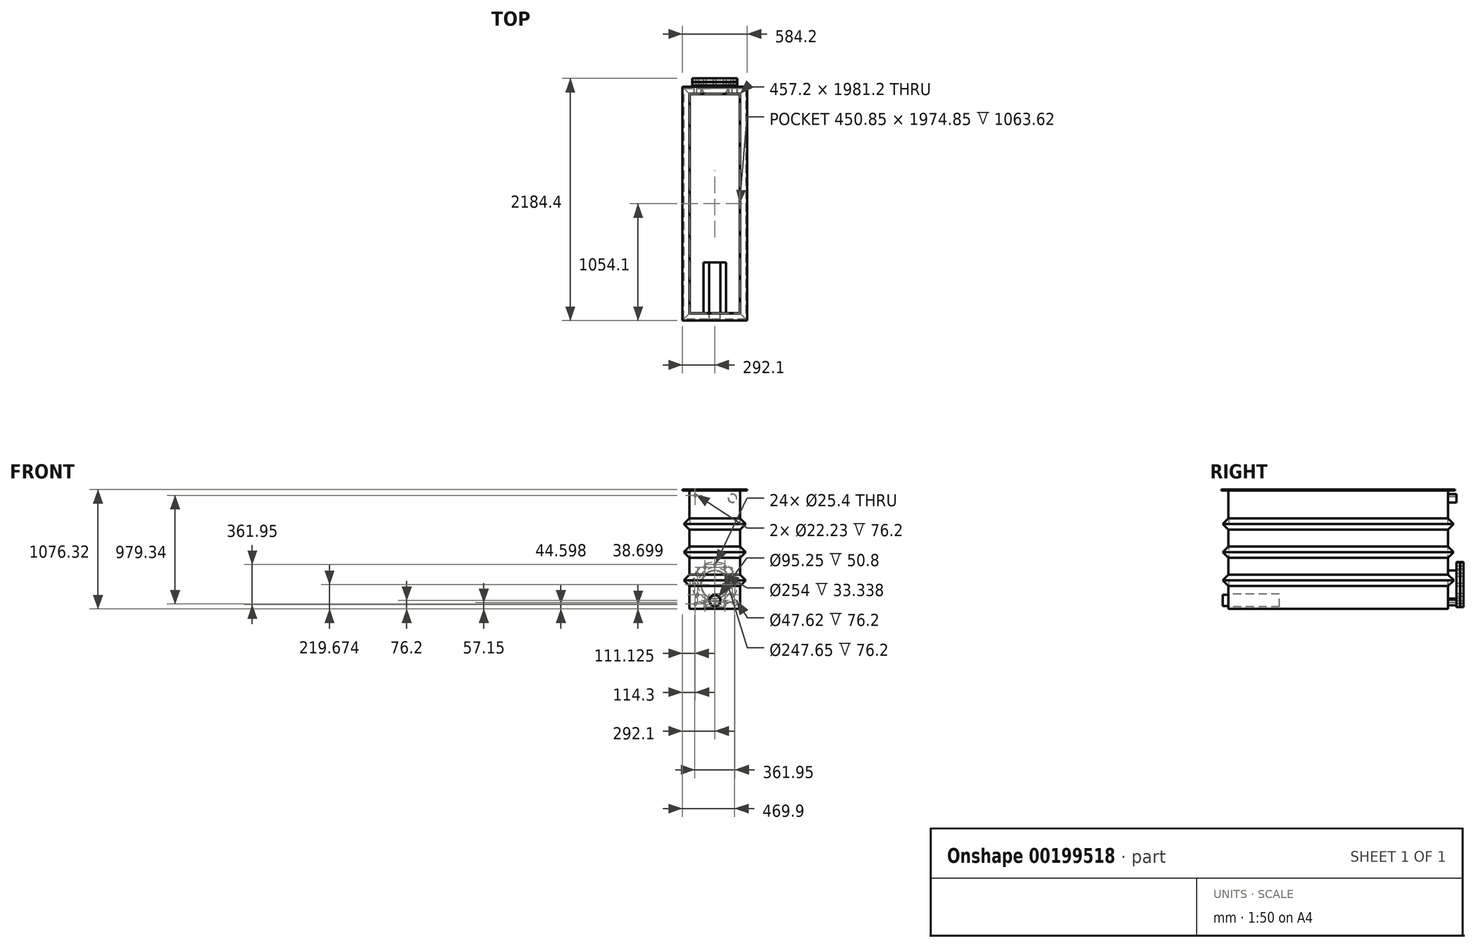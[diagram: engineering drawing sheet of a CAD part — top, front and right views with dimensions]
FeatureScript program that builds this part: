
annotation { "Feature Type Name" : "Feature", "Feature Type Description" : "" }
export const myFeature = defineFeature(function(context is Context, id is Id, definition is map)
    precondition{}
    {
        {
            var Q0;
            Q0=qCreatedBy(makeId("Right.planeOp"),FACE);
            var sketch = newSketch(context, id + "F0", { "sketchPlane" : qUnion([Q0])});
            skLineSegment(sketch, "E0.bottom", {"start": v(-990.6, 533.4) * mm, "end": v(990.6, 533.4) * mm});
            skLineSegment(sketch, "E0.top", {"start": v(-990.6, -533.4) * mm, "end": v(990.6, -533.4) * mm});
            skLineSegment(sketch, "E0.left", {"start": v(-990.6, 533.4) * mm, "end": v(-990.6, -533.4) * mm});
            skLineSegment(sketch, "E0.right", {"start": v(990.6, 533.4) * mm, "end": v(990.6, -533.4) * mm});
            skSolve(sketch);
        }
        {
            var Q0;
            Q0=makeQuery(id+"F0.imprint","IMPRINT",FACE,{"disambiguationData":[TD([[makeQuery(id+"F0.imprint","IMPRINT",EDGE,{"derivedFrom":sQuery(id+"F0.wireOp",EDGE,"E0.bottom")}),-1.0]])]});
            extrude(context, id + "F1", {"entities" : qUnion([Q0]), "endBound" : BoundingType.SYMMETRIC, "depth" : 457.2 * mm, "hasSecondDirection" : true, "secondDirectionOppositeDirection" : true, "secondDirectionDepth" : 228.6 * mm});
        }
        {
            var Q0;
            Q0=makeQuery(id+"F1.opExtrude","SWEPT_FACE",FACE,{"disambiguationData":[OSD([sQuery(id+"F0.wireOp",EDGE,"E0.bottom")])]});
            shell(context, id + "F2", {"entities" : qUnion([Q0]), "thickness" : 3.17 * mm});
        }
        {
            var Q0;
            Q0=makeQuery(id+"F1.opExtrude","SWEPT_FACE",FACE,{"disambiguationData":[OSD([sQuery(id+"F0.wireOp",EDGE,"E0.left")])]});
            var sketch = newSketch(context, id + "F3", { "sketchPlane" : qUnion([Q0])});
            skCircle(sketch, "E1", {"center": v(0, -457.2) * mm, "radius": 50.8 * mm});
            skCircle(sketch, "E2", {"center": v(0, -457.2) * mm, "radius": 47.63 * mm});
            skLineSegment(sketch, "E3", {"start": v(-571.69, -330.2) * mm, "end": v(666.68, -330.2) * mm, "construction": true});
            skSolve(sketch);
        }
        {
            var Q0;
            Q0 = qSketchRegion(id + "F3", true);
            extrude(context, id + "F4", {"entities" : qUnion([Q0]), "depth" : 50.8 * mm});
        }
        {
            var Q0;
            Q0=makeQuery(id+"F2.opShell","OFFSET_FACE",FACE,{"disambiguationData":[OSD([sQuery(id+"F0.wireOp",EDGE,"E0.left")])]});
            var sketch = newSketch(context, id + "F5", { "sketchPlane" : qUnion([Q0])});
            skPoint(sketch, "E4", {"position": v(0, -457.2) * mm});
            skCircle(sketch, "E5", {"center": v(0, -457.2) * mm, "radius": 38.1 * mm, "construction": true});
            skLineSegment(sketch, "E6", {"start": v(-101.6, -514.35) * mm, "end": v(-50.8, -400.05) * mm});
            skLineSegment(sketch, "E7", {"start": v(-50.8, -400.05) * mm, "end": v(50.8, -400.05) * mm});
            skLineSegment(sketch, "E8", {"start": v(50.8, -400.05) * mm, "end": v(101.6, -514.35) * mm});
            skLineSegment(sketch, "E9", {"start": v(101.6, -514.35) * mm, "end": v(-101.6, -514.35) * mm});
            skSolve(sketch);
        }
        {
            var Q0;
            Q0=makeQuery(id+"F5.imprint","IMPRINT",FACE,{"disambiguationData":[TD([[makeQuery(id+"F5.imprint","IMPRINT",EDGE,{"derivedFrom":sQuery(id+"F5.wireOp",EDGE,"E6")}),-1.0]])]});
            extrude(context, id + "F6", {"entities" : qUnion([Q0]), "operationType" : NewBodyOperationType.ADD, "depth" : 457.2 * mm});
        }
        {
            var Q0;
            Q0=makeQuery(id+"F1.opExtrude","SWEPT_FACE",FACE,{"disambiguationData":[OSD([sQuery(id+"F0.wireOp",EDGE,"E0.right")])]});
            var sketch = newSketch(context, id + "F7", { "sketchPlane" : qUnion([Q0])});
            skPoint(sketch, "E10", {"position": v(0, -313.73) * mm});
            skCircle(sketch, "E11", {"center": v(0, -313.73) * mm, "radius": 127 * mm});
            skCircle(sketch, "E12", {"center": v(0, -313.73) * mm, "radius": 123.83 * mm});
            skSolve(sketch);
        }
        {
            var Q0;
            Q0 = qSketchRegion(id + "F7", true);
            extrude(context, id + "F8", {"entities" : qUnion([Q0]), "operationType" : NewBodyOperationType.ADD, "depth" : 76.2 * mm});
        }
        {
            var Q0;
            Q0=makeQuery(id+"F8.opExtrude","CAP_FACE",FACE,{"disambiguationData":[OSD([sQuery(id+"F7.wireOp",EDGE,"E11"),sQuery(id+"F7.wireOp",EDGE,"E12")])],"isStart":false});
            var sketch = newSketch(context, id + "F9", { "sketchPlane" : qUnion([Q0])});
            skPoint(sketch, "E13", {"position": v(0, -313.73) * mm});
            skCircle(sketch, "E14", {"center": v(0, -313.73) * mm, "radius": 203.2 * mm});
            skCircle(sketch, "E15", {"center": v(0, -313.73) * mm, "radius": 123.83 * mm});
            skSolve(sketch);
        }
        {
            var Q0;
            Q0=makeQuery(id+"F9.imprint","IMPRINT",FACE,{"disambiguationData":[TD([[makeQuery(id+"F9.imprint","IMPRINT",EDGE,{"derivedFrom":sQuery(id+"F9.wireOp",EDGE,"E14")}),1.0]])]});
            extrude(context, id + "F10", {"entities" : qUnion([Q0]), "depth" : 30.16 * mm});
        }
        {
            var Q0;
            Q0=makeQuery(id+"F10.opExtrude","CAP_FACE",FACE,{"disambiguationData":[OSD([sQuery(id+"F7.wireOp",EDGE,"E11"),sQuery(id+"F9.wireOp",EDGE,"E14")])],"isStart":false});
            var sketch = newSketch(context, id + "F11", { "sketchPlane" : qUnion([Q0])});
            skPoint(sketch, "E16", {"position": v(0, -313.73) * mm});
            skCircle(sketch, "E17", {"center": v(0, -132.75) * mm, "radius": 12.7 * mm});
            skCircle(sketch, "E18.1.0", {"center": v(-90.49, -157) * mm, "radius": 12.7 * mm});
            skCircle(sketch, "E18.2.0", {"center": v(-156.73, -223.24) * mm, "radius": 12.7 * mm});
            skCircle(sketch, "E18.3.0", {"center": v(-180.98, -313.73) * mm, "radius": 12.7 * mm});
            skCircle(sketch, "E18.4.0", {"center": v(-156.73, -404.21) * mm, "radius": 12.7 * mm});
            skCircle(sketch, "E18.5.0", {"center": v(-90.49, -470.45) * mm, "radius": 12.7 * mm});
            skCircle(sketch, "E18.6.0", {"center": v(0, -494.7) * mm, "radius": 12.7 * mm});
            skCircle(sketch, "E18.7.0", {"center": v(90.49, -470.45) * mm, "radius": 12.7 * mm});
            skCircle(sketch, "E18.8.0", {"center": v(156.73, -404.21) * mm, "radius": 12.7 * mm});
            skCircle(sketch, "E18.9.0", {"center": v(180.98, -313.73) * mm, "radius": 12.7 * mm});
            skCircle(sketch, "E19.1.10.0", {"center": v(156.73, -223.24) * mm, "radius": 12.7 * mm});
            skCircle(sketch, "E19.1.11.0", {"center": v(90.49, -157) * mm, "radius": 12.7 * mm});
            skSolve(sketch);
        }
        {
            var Q0;
            Q0 = qSketchRegion(id + "F11", true);
            extrude(context, id + "F12", {"entities" : qUnion([Q0]), "operationType" : NewBodyOperationType.REMOVE, "endBound" : BoundingType.UP_TO_NEXT, "oppositeDirection" : true, "depth" : 25.4 * mm});
        }
        {
            var Q0;
            Q0=makeQuery(id+"F10.opExtrude","CAP_FACE",FACE,{"disambiguationData":[OSD([sQuery(id+"F7.wireOp",EDGE,"E11"),sQuery(id+"F9.wireOp",EDGE,"E14")])],"isStart":false});
            var sketch = newSketch(context, id + "F13", { "sketchPlane" : qUnion([Q0])});
            skSolve(sketch);
        }
        {
            var Q0;
            Q0=makeQuery(id+"F13.imprint","IMPRINT",FACE,{"disambiguationData":[TD([[makeQuery(id+"F13.imprint","IMPRINT",EDGE,{"derivedFrom":makeQuery(id+"F10.opExtrude","CAP_EDGE",EDGE,{"disambiguationData":[OSD([sQuery(id+"F9.wireOp",EDGE,"E14")])],"isStart":false})}),1.0]])]});
            var sketch = newSketch(context, id + "F14", { "sketchPlane" : qUnion([Q0])});
            skPoint(sketch, "E20", {"position": v(0, -313.73) * mm});
            skCircle(sketch, "E21", {"center": v(0, -313.73) * mm, "radius": 127 * mm});
            skCircle(sketch, "E22", {"center": v(0, -313.73) * mm, "radius": 152.4 * mm});
            skSolve(sketch);
        }
        {
            var Q0;
            Q0 = qSketchRegion(id + "F14", true);
            extrude(context, id + "F15", {"entities" : qUnion([Q0]), "operationType" : NewBodyOperationType.ADD, "depth" : 3.17 * mm});
        }
        {
            var Q0;
            Q0=makeQuery(id+"F15.opExtrude","CAP_FACE",FACE,{"disambiguationData":[OSD([sQuery(id+"F14.wireOp",EDGE,"E21"),sQuery(id+"F14.wireOp",EDGE,"E22")])],"isStart":false});
            var sketch = newSketch(context, id + "F16", { "sketchPlane" : qUnion([Q0])});
            skPoint(sketch, "E23", {"position": v(0, -313.73) * mm});
            skCircle(sketch, "E24", {"center": v(0, -313.73) * mm, "radius": 203.2 * mm});
            skSolve(sketch);
        }
        {
            var Q0;
            Q0 = qSketchRegion(id + "F16", true);
            extrude(context, id + "F17", {"entities" : qUnion([Q0]), "operationType" : NewBodyOperationType.ADD, "depth" : 30.16 * mm});
        }
        {
            var Q0;
            Q0=makeQuery(id+"F17.opExtrude","CAP_FACE",FACE,{"disambiguationData":[OSD([sQuery(id+"F16.wireOp",EDGE,"E24")])],"isStart":false});
            var sketch = newSketch(context, id + "F18", { "sketchPlane" : qUnion([Q0])});
            skPoint(sketch, "E25", {"position": v(0, -313.73) * mm});
            skCircle(sketch, "E26", {"center": v(0, -132.75) * mm, "radius": 12.7 * mm});
            skCircle(sketch, "E27.1.0", {"center": v(-90.49, -157) * mm, "radius": 12.7 * mm});
            skCircle(sketch, "E27.2.0", {"center": v(-156.73, -223.24) * mm, "radius": 12.7 * mm});
            skCircle(sketch, "E27.3.0", {"center": v(-180.98, -313.73) * mm, "radius": 12.7 * mm});
            skCircle(sketch, "E27.4.0", {"center": v(-156.73, -404.21) * mm, "radius": 12.7 * mm});
            skCircle(sketch, "E27.5.0", {"center": v(-90.49, -470.45) * mm, "radius": 12.7 * mm});
            skCircle(sketch, "E27.6.0", {"center": v(0, -494.7) * mm, "radius": 12.7 * mm});
            skCircle(sketch, "E27.7.0", {"center": v(90.49, -470.45) * mm, "radius": 12.7 * mm});
            skCircle(sketch, "E27.8.0", {"center": v(156.73, -404.21) * mm, "radius": 12.7 * mm});
            skCircle(sketch, "E27.9.0", {"center": v(180.98, -313.73) * mm, "radius": 12.7 * mm});
            skCircle(sketch, "E28.1.10.0", {"center": v(156.73, -223.24) * mm, "radius": 12.7 * mm});
            skCircle(sketch, "E28.1.11.0", {"center": v(90.49, -157) * mm, "radius": 12.7 * mm});
            skSolve(sketch);
        }
        {
            var Q0;
            Q0 = qSketchRegion(id + "F18", true);
            extrude(context, id + "F19", {"entities" : qUnion([Q0]), "operationType" : NewBodyOperationType.REMOVE, "endBound" : BoundingType.UP_TO_NEXT, "oppositeDirection" : true, "depth" : 25.4 * mm});
        }
        {
            var Q0;
            {var subQ1=sQuery(id+"F0.wireOp",EDGE,"E0.right");var subQ3=sQuery(id+"F0.wireOp",EDGE,"E0.bottom");Q0=makeQuery(id+"F8.boolean.opBoolean","SPLIT",FACE,{"disambiguationData":[TD([makeQuery(id+"F1.opExtrude","SWEPT_FACE",FACE,{"disambiguationData":[OSD([subQ3])]})])],"derivedFrom":makeQuery(id+"F1.opExtrude","SWEPT_FACE",FACE,{"disambiguationData":[OSD([subQ1])]})});}
            var sketch = newSketch(context, id + "F20", { "sketchPlane" : qUnion([Q0])});
            skPoint(sketch, "E29", {"position": v(0, -409.57) * mm});
            skPoint(sketch, "E30", {"position": v(-158.75, 465.14) * mm});
            skCircle(sketch, "E31", {"center": v(-158.75, 465.14) * mm, "radius": 38.1 * mm});
            skCircle(sketch, "E32", {"center": v(-158.75, 465.14) * mm, "radius": 36.51 * mm});
            skPoint(sketch, "E33", {"position": v(-158.75, 428.63) * mm});
            skCircle(sketch, "E34", {"center": v(-177.8, -476.25) * mm, "radius": 25.4 * mm});
            skCircle(sketch, "E35", {"center": v(-177.8, -476.25) * mm, "radius": 23.81 * mm});
            skCircle(sketch, "E36", {"center": v(177.8, 490.54) * mm, "radius": 12.7 * mm});
            skCircle(sketch, "E37", {"center": v(177.8, 490.54) * mm, "radius": 11.11 * mm});
            skCircle(sketch, "E38", {"center": v(177.8, -488.8) * mm, "radius": 12.7 * mm});
            skCircle(sketch, "E39", {"center": v(177.8, -488.8) * mm, "radius": 11.11 * mm});
            skLineSegment(sketch, "E40", {"start": v(-180.53, -501.5) * mm, "end": v(332.18, -501.5) * mm, "construction": true});
            skLineSegment(sketch, "E41", {"start": v(-158.75, 503.24) * mm, "end": v(393.96, 503.24) * mm, "construction": true});
            skLineSegment(sketch, "E42", {"start": v(-158.75, 465.14) * mm, "end": v(-158.75, 301.65) * mm, "construction": true});
            skSolve(sketch);
        }
        {
            var Q0;
            Q0 = qSketchRegion(id + "F20", true);
            extrude(context, id + "F21", {"entities" : qUnion([Q0]), "operationType" : NewBodyOperationType.ADD, "depth" : 76.2 * mm});
        }
        {
            var Q0;
            Q0=makeQuery(id+"F2.opShell","OFFSET_FACE",FACE,{"disambiguationData":[OSD([sQuery(id+"F0.wireOp",EDGE,"E0.top")])]});
            cPlane(context, id + "F22", {"entities" : qUnion([Q0]), "cplaneType" : CPlaneType.OFFSET, "offset" : 254 * mm, "width" : 152.4 * mm, "height" : 152.4 * mm});
        }
        {
            var Q0;
            Q0=qCreatedBy(id+"F22.planeOp",FACE);
            var sketch = newSketch(context, id + "F23", { "sketchPlane" : qUnion([Q0])});
            skPoint(sketch, "E43", {"position": v(-225.43, 987.43) * mm});
            skPoint(sketch, "E44", {"position": v(228.6, 990.6) * mm});
            skPoint(sketch, "E45", {"position": v(228.6, -990.6) * mm});
            skPoint(sketch, "E46", {"position": v(-228.6, -990.6) * mm});
            skLineSegment(sketch, "E47", {"start": v(-228.6, -990.6) * mm, "end": v(-225.42, 987.43) * mm});
            skLineSegment(sketch, "E48", {"start": v(228.6, 990.6) * mm, "end": v(228.6, -990.6) * mm});
            skLineSegment(sketch, "E49", {"start": v(-225.42, 987.43) * mm, "end": v(228.6, 990.6) * mm});
            skLineSegment(sketch, "E50", {"start": v(-228.6, -990.6) * mm, "end": v(228.6, -990.6) * mm});
            skSolve(sketch);
        }
        {
            var Q0;
            Q0=makeQuery(id+"F1.opExtrude","SWEPT_FACE",FACE,{"disambiguationData":[OSD([sQuery(id+"F0.wireOp",EDGE,"E0.left")])]});
            var sketch = newSketch(context, id + "F24", { "sketchPlane" : qUnion([Q0])});
            skLineSegment(sketch, "E51", {"start": v(-228.6, -276.22) * mm, "end": v(-228.6, -327.02) * mm});
            skLineSegment(sketch, "E52", {"start": v(-228.6, -327.02) * mm, "end": v(-279.4, -276.22) * mm});
            skLineSegment(sketch, "E53", {"start": v(-279.4, -276.22) * mm, "end": v(-228.6, -225.42) * mm});
            skLineSegment(sketch, "E54", {"start": v(-228.6, -225.42) * mm, "end": v(-228.6, -276.22) * mm});
            skSolve(sketch);
        }
        {
            var Q0;
            Q0=makeQuery(id+"F24.imprint","IMPRINT",FACE,{"disambiguationData":[TD([[makeQuery(id+"F24.imprint","IMPRINT",EDGE,{"derivedFrom":sQuery(id+"F24.wireOp",EDGE,"E51")}),-1.0]])]});
            var Q1;
            Q1=sQuery(id+"F23.wireOp",EDGE,"E47");
            var Q2;
            Q2=sQuery(id+"F23.wireOp",EDGE,"E49");
            var Q3;
            Q3=sQuery(id+"F23.wireOp",EDGE,"E48");
            var Q4;
            Q4=sQuery(id+"F23.wireOp",EDGE,"E50");
            sweep(context, id + "F25", {"operationType" : NewBodyOperationType.ADD, "profiles" : qUnion([Q0]), "path" : qUnion([Q1, Q2, Q3, Q4])});
        }
        {
            var Q0;
            Q0=qCreatedBy(id+"F22.planeOp",FACE);
            cPlane(context, id + "F26", {"entities" : qUnion([Q0]), "cplaneType" : CPlaneType.OFFSET, "offset" : 254 * mm, "width" : 152.4 * mm, "height" : 152.4 * mm});
        }
        {
            var Q0;
            Q0=qCreatedBy(id+"F26.planeOp",FACE);
            var sketch = newSketch(context, id + "F27", { "sketchPlane" : qUnion([Q0])});
            skPoint(sketch, "E55", {"position": v(-228.6, 990.6) * mm});
            skPoint(sketch, "E56", {"position": v(228.6, 990.6) * mm});
            skPoint(sketch, "E57", {"position": v(228.6, -990.6) * mm});
            skPoint(sketch, "E58", {"position": v(-228.6, -990.6) * mm});
            skLineSegment(sketch, "E59", {"start": v(-228.6, -990.6) * mm, "end": v(-228.6, 990.6) * mm});
            skLineSegment(sketch, "E60", {"start": v(-228.6, 990.6) * mm, "end": v(228.6, 990.6) * mm});
            skLineSegment(sketch, "E61", {"start": v(228.6, 990.6) * mm, "end": v(228.6, -990.6) * mm});
            skLineSegment(sketch, "E62", {"start": v(228.6, -990.6) * mm, "end": v(-228.6, -990.6) * mm});
            skSolve(sketch);
        }
        {
            var Q0;
            {var subQ1=sQuery(id+"F0.wireOp",EDGE,"E0.left");var subQ3=sQuery(id+"F0.wireOp",EDGE,"E0.bottom");Q0=makeQuery(id+"F25.boolean.opBoolean","SPLIT",FACE,{"disambiguationData":[TD([makeQuery(id+"F1.opExtrude","SWEPT_FACE",FACE,{"disambiguationData":[OSD([subQ3])]})])],"derivedFrom":makeQuery(id+"F1.opExtrude","SWEPT_FACE",FACE,{"disambiguationData":[OSD([subQ1])]})});}
            var sketch = newSketch(context, id + "F28", { "sketchPlane" : qUnion([Q0])});
            skPoint(sketch, "E63", {"position": v(-228.6, -22.22) * mm});
            skLineSegment(sketch, "E64", {"start": v(-228.6, -22.22) * mm, "end": v(-228.6, -73.02) * mm});
            skLineSegment(sketch, "E65", {"start": v(-228.6, -73.02) * mm, "end": v(-279.4, -22.22) * mm});
            skLineSegment(sketch, "E66", {"start": v(-279.4, -22.22) * mm, "end": v(-228.6, 28.58) * mm});
            skLineSegment(sketch, "E67", {"start": v(-228.6, 28.58) * mm, "end": v(-228.6, -22.22) * mm});
            skSolve(sketch);
        }
        {
            var Q0;
            Q0=qCreatedBy(id+"F26.planeOp",FACE);
            cPlane(context, id + "F29", {"entities" : qUnion([Q0]), "cplaneType" : CPlaneType.OFFSET, "offset" : 254 * mm, "width" : 152.4 * mm, "height" : 152.4 * mm});
        }
        {
            var Q0;
            Q0=qCreatedBy(id+"F29.planeOp",FACE);
            var sketch = newSketch(context, id + "F30", { "sketchPlane" : qUnion([Q0])});
            skPoint(sketch, "E68", {"position": v(-228.6, 990.6) * mm});
            skPoint(sketch, "E69", {"position": v(228.6, 990.6) * mm});
            skPoint(sketch, "E70", {"position": v(228.6, -990.6) * mm});
            skPoint(sketch, "E71", {"position": v(-228.6, -990.6) * mm});
            skLineSegment(sketch, "E72", {"start": v(-228.6, -990.6) * mm, "end": v(-228.6, 990.6) * mm});
            skLineSegment(sketch, "E73", {"start": v(-228.6, 990.6) * mm, "end": v(228.6, 990.6) * mm});
            skLineSegment(sketch, "E74", {"start": v(228.6, 990.6) * mm, "end": v(228.6, -990.6) * mm});
            skLineSegment(sketch, "E75", {"start": v(228.6, -990.6) * mm, "end": v(-228.6, -990.6) * mm});
            skSolve(sketch);
        }
        {
            var Q0;
            {var subQ2=sQuery(id+"F0.wireOp",EDGE,"E0.left");var subQ4=sQuery(id+"F0.wireOp",EDGE,"E0.bottom");var subQ7=makeQuery(id+"F1.opExtrude","SWEPT_FACE",FACE,{"disambiguationData":[OSD([subQ4])]});Q0=makeQuery(id+"FEdXTNuG9fACU3v_4.boolean.opBoolean","SPLIT",FACE,{"disambiguationData":[TD([subQ7])],"derivedFrom":makeQuery(id+"F25.boolean.opBoolean","SPLIT",FACE,{"disambiguationData":[TD([subQ7])],"derivedFrom":makeQuery(id+"F1.opExtrude","SWEPT_FACE",FACE,{"disambiguationData":[OSD([subQ2])]})})});}
            var sketch = newSketch(context, id + "F31", { "sketchPlane" : qUnion([Q0])});
            skPoint(sketch, "E76", {"position": v(-228.6, 231.78) * mm});
            skLineSegment(sketch, "E77", {"start": v(-228.6, 231.78) * mm, "end": v(-228.6, 180.98) * mm});
            skLineSegment(sketch, "E78", {"start": v(-228.6, 180.98) * mm, "end": v(-279.4, 231.78) * mm});
            skLineSegment(sketch, "E79", {"start": v(-279.4, 231.78) * mm, "end": v(-228.6, 282.58) * mm});
            skLineSegment(sketch, "E80", {"start": v(-228.6, 282.58) * mm, "end": v(-228.6, 231.78) * mm});
            skSolve(sketch);
        }
        {
            var Q0;
            Q0=makeQuery(id+"F31.imprint","IMPRINT",FACE,{"disambiguationData":[TD([[makeQuery(id+"F31.imprint","IMPRINT",EDGE,{"derivedFrom":sQuery(id+"F31.wireOp",EDGE,"E77")}),-1.0]])]});
            var Q1;
            Q1=sQuery(id+"F30.wireOp",EDGE,"E72");
            var Q2;
            Q2=sQuery(id+"F30.wireOp",EDGE,"E73");
            var Q3;
            Q3=sQuery(id+"F30.wireOp",EDGE,"E74");
            var Q4;
            Q4=sQuery(id+"F30.wireOp",EDGE,"E75");
            sweep(context, id + "F32", {"operationType" : NewBodyOperationType.ADD, "profiles" : qUnion([Q0]), "path" : qUnion([Q1, Q2, Q3, Q4])});
        }
        {
            var Q0;
            Q0=makeQuery(id+"F1.opExtrude","SWEPT_FACE",FACE,{"disambiguationData":[OSD([sQuery(id+"F0.wireOp",EDGE,"E0.bottom")])]});
            var sketch = newSketch(context, id + "F33", { "sketchPlane" : qUnion([Q0])});
            skPoint(sketch, "E81", {"position": v(-292.1, 1054.1) * mm});
            skPoint(sketch, "E82", {"position": v(292.1, -1054.1) * mm});
            skLineSegment(sketch, "E83.bottom", {"start": v(-225.43, 987.43) * mm, "end": v(225.42, 987.43) * mm});
            skLineSegment(sketch, "E83.top", {"start": v(-225.42, -987.43) * mm, "end": v(225.43, -987.43) * mm});
            skLineSegment(sketch, "E83.left", {"start": v(-225.43, 987.43) * mm, "end": v(-225.42, -987.43) * mm});
            skLineSegment(sketch, "E83.right", {"start": v(225.42, 987.43) * mm, "end": v(225.43, -987.43) * mm});
            skLineSegment(sketch, "E84.bottom", {"start": v(-292.1, 1054.1) * mm, "end": v(292.1, 1054.1) * mm});
            skLineSegment(sketch, "E84.top", {"start": v(-292.1, -1054.1) * mm, "end": v(292.1, -1054.1) * mm});
            skLineSegment(sketch, "E84.left", {"start": v(-292.1, 1054.1) * mm, "end": v(-292.1, -1054.1) * mm});
            skLineSegment(sketch, "E84.right", {"start": v(292.1, 1054.1) * mm, "end": v(292.1, -1054.1) * mm});
            skSolve(sketch);
        }
        {
            var Q0;
            Q0=makeQuery(id+"F28.imprint","IMPRINT",FACE,{"disambiguationData":[TD([[makeQuery(id+"F28.imprint","IMPRINT",EDGE,{"derivedFrom":sQuery(id+"F28.wireOp",EDGE,"E64")}),-1.0]])]});
            var Q1;
            Q1=sQuery(id+"F27.wireOp",EDGE,"E59");
            var Q2;
            Q2=sQuery(id+"F27.wireOp",EDGE,"E60");
            var Q3;
            Q3=sQuery(id+"F27.wireOp",EDGE,"E61");
            var Q4;
            Q4=sQuery(id+"F27.wireOp",EDGE,"E62");
            sweep(context, id + "F34", {"operationType" : NewBodyOperationType.ADD, "profiles" : qUnion([Q0]), "path" : qUnion([Q1, Q2, Q3, Q4])});
        }
        {
            var Q0;
            Q0=makeQuery(id+"F33.imprint","IMPRINT",FACE,{"disambiguationData":[TD([[makeQuery(id+"F33.imprint","IMPRINT",EDGE,{"derivedFrom":sQuery(id+"F33.wireOp",EDGE,"E84.bottom")}),-1.0]])]});
            extrude(context, id + "F35", {"entities" : qUnion([Q0]), "depth" : 9.52 * mm});
        }
    });
